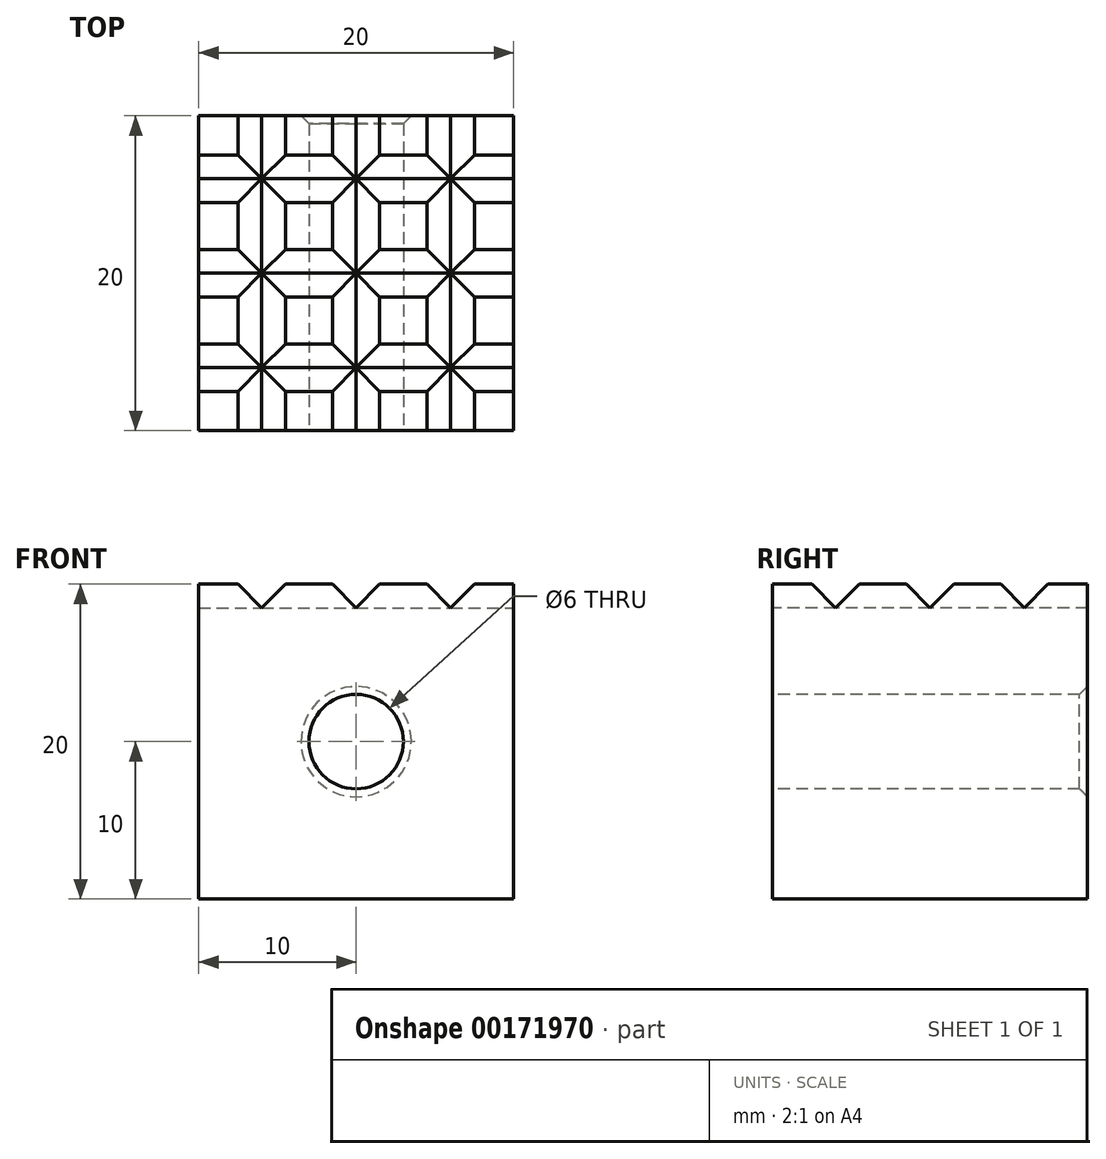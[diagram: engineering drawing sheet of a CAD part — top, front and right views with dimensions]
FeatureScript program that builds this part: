
annotation { "Feature Type Name" : "Feature", "Feature Type Description" : "" }
export const myFeature = defineFeature(function(context is Context, id is Id, definition is map)
    precondition{}
    {
        {
            var Q0;
            Q0=qCreatedBy(makeId("Top.planeOp"),FACE);
            var sketch = newSketch(context, id + "F0", { "sketchPlane" : qUnion([Q0])});
            skLineSegment(sketch, "E0.bottom", {"start": v(10, 10) * mm, "end": v(-10, 10) * mm});
            skLineSegment(sketch, "E0.top", {"start": v(10, -10) * mm, "end": v(-10, -10) * mm});
            skLineSegment(sketch, "E0.left", {"start": v(10, 10) * mm, "end": v(10, -10) * mm});
            skLineSegment(sketch, "E0.right", {"start": v(-10, 10) * mm, "end": v(-10, -10) * mm});
            skPoint(sketch, "E0.middle", {"position": v(0, 0) * mm});
            skSolve(sketch);
        }
        {
            var Q0;
            Q0 = qSketchRegion(id + "F0", true);
            extrude(context, id + "F1", {"entities" : qUnion([Q0]), "endBound" : BoundingType.SYMMETRIC, "depth" : 20 * mm});
        }
        {
            var Q0;
            Q0=makeQuery(id+"F1.opExtrude","SWEPT_FACE",FACE,{"disambiguationData":[OSD([sQuery(id+"F0.wireOp",EDGE,"E0.top")])]});
            var sketch = newSketch(context, id + "F2", { "sketchPlane" : qUnion([Q0])});
            skCircle(sketch, "E1", {"center": v(0, 0) * mm, "radius": 3 * mm});
            skSolve(sketch);
        }
        {
            var Q0;
            Q0=makeQuery(id+"F2.imprint","IMPRINT",FACE,{"disambiguationData":[TD([[makeQuery(id+"F2.imprint","IMPRINT",EDGE,{"derivedFrom":sQuery(id+"F2.wireOp",EDGE,"E1")}),1.0]])]});
            extrude(context, id + "F3", {"entities" : qUnion([Q0]), "operationType" : NewBodyOperationType.REMOVE, "oppositeDirection" : true, "depth" : 25 * mm});
        }
        {
            var Q0;
            Q0=makeQuery(id+"F3.boolean.opBoolean","COPY",EDGE,{"derivedFrom":makeQuery(id+"F3.opExtrude","CAP_EDGE",EDGE,{"disambiguationData":[OSD([sQuery(id+"F2.wireOp",EDGE,"E1")])],"isStart":true})});
            var Q1;
            Q1=makeQuery(id+"F3.boolean.opBoolean","INTERSECT",EDGE,{"derivedFrom":[makeQuery(id+"F1.opExtrude","SWEPT_FACE",FACE,{"disambiguationData":[OSD([sQuery(id+"F0.wireOp",EDGE,"E0.bottom")])]}),makeQuery(id+"F3.opExtrude","SWEPT_FACE",FACE,{"disambiguationData":[OSD([sQuery(id+"F2.wireOp",EDGE,"E1")])]})]});
            chamfer(context, id + "F4", {"entities" : qUnion([Q0, Q1]), "chamferType" : ChamferType.OFFSET_ANGLE, "width" : .5 * mm, "oppositeDirection" : false, "angle" : 45 * degree, "tangentPropagation" : true});
        }
        {
            var Q0;
            Q0=makeQuery(id+"F1.opExtrude","SWEPT_FACE",FACE,{"disambiguationData":[OSD([sQuery(id+"F0.wireOp",EDGE,"E0.top")])]});
            var sketch = newSketch(context, id + "F5", { "sketchPlane" : qUnion([Q0])});
            skLineSegment(sketch, "E2", {"start": v(4.5, 10) * mm, "end": v(6, 8.5) * mm});
            skLineSegment(sketch, "E3", {"start": v(6, 8.5) * mm, "end": v(7.5, 10) * mm});
            skLineSegment(sketch, "E4", {"start": v(7.5, 10) * mm, "end": v(4.5, 10) * mm});
            skLineSegment(sketch, "E5.1.0.0", {"start": v(1.5, 10) * mm, "end": v(-1.5, 10) * mm});
            skLineSegment(sketch, "E5.1.0.1", {"start": v(0, 8.5) * mm, "end": v(1.5, 10) * mm});
            skLineSegment(sketch, "E5.1.0.2", {"start": v(-1.5, 10) * mm, "end": v(0, 8.5) * mm});
            skLineSegment(sketch, "E5.2.0.0", {"start": v(-4.5, 10) * mm, "end": v(-7.5, 10) * mm});
            skLineSegment(sketch, "E5.2.0.1", {"start": v(-6, 8.5) * mm, "end": v(-4.5, 10) * mm});
            skLineSegment(sketch, "E5.2.0.2", {"start": v(-7.5, 10) * mm, "end": v(-6, 8.5) * mm});
            skLineSegment(sketch, "E5.direction1", {"start": v(6, 8.5) * mm, "end": v(0, 8.5) * mm, "construction": true});
            skSolve(sketch);
        }
        {
            var Q0;
            Q0 = qSketchRegion(id + "F5", true);
            extrude(context, id + "F6", {"entities" : qUnion([Q0]), "operationType" : NewBodyOperationType.REMOVE, "oppositeDirection" : true, "depth" : 25 * mm});
        }
        {
            var Q0;
            Q0=makeQuery(id+"F1.opExtrude","SWEPT_FACE",FACE,{"disambiguationData":[OSD([sQuery(id+"F0.wireOp",EDGE,"E0.left")])]});
            var sketch = newSketch(context, id + "F7", { "sketchPlane" : qUnion([Q0])});
            skLineSegment(sketch, "E6", {"start": v(4.5, 10) * mm, "end": v(6, 8.5) * mm});
            skLineSegment(sketch, "E7", {"start": v(6, 8.5) * mm, "end": v(7.5, 10) * mm});
            skLineSegment(sketch, "E8", {"start": v(7.5, 10) * mm, "end": v(4.5, 10) * mm});
            skLineSegment(sketch, "E9.1.0.0", {"start": v(1.5, 10) * mm, "end": v(-1.5, 10) * mm});
            skLineSegment(sketch, "E9.1.0.1", {"start": v(0, 8.5) * mm, "end": v(1.5, 10) * mm});
            skLineSegment(sketch, "E9.1.0.2", {"start": v(-1.5, 10) * mm, "end": v(0, 8.5) * mm});
            skLineSegment(sketch, "E9.2.0.0", {"start": v(-4.5, 10) * mm, "end": v(-7.5, 10) * mm});
            skLineSegment(sketch, "E9.2.0.1", {"start": v(-6, 8.5) * mm, "end": v(-4.5, 10) * mm});
            skLineSegment(sketch, "E9.2.0.2", {"start": v(-7.5, 10) * mm, "end": v(-6, 8.5) * mm});
            skLineSegment(sketch, "E9.direction1", {"start": v(6, 8.5) * mm, "end": v(0, 8.5) * mm, "construction": true});
            skSolve(sketch);
        }
        {
            var Q0;
            Q0=makeQuery(id+"F7.imprint","IMPRINT",FACE,{"disambiguationData":[TD([[makeQuery(id+"F7.imprint","IMPRINT",EDGE,{"derivedFrom":sQuery(id+"F7.wireOp",EDGE,"E9.2.0.0")}),1.0]])]});
            var Q1;
            Q1=makeQuery(id+"F7.imprint","IMPRINT",FACE,{"disambiguationData":[TD([[makeQuery(id+"F7.imprint","IMPRINT",EDGE,{"derivedFrom":sQuery(id+"F7.wireOp",EDGE,"E9.1.0.0")}),1.0]])]});
            var Q2;
            Q2=makeQuery(id+"F7.imprint","IMPRINT",FACE,{"disambiguationData":[TD([[makeQuery(id+"F7.imprint","IMPRINT",EDGE,{"derivedFrom":sQuery(id+"F7.wireOp",EDGE,"E6")}),1.0]])]});
            extrude(context, id + "F8", {"entities" : qUnion([Q0, Q1, Q2]), "operationType" : NewBodyOperationType.REMOVE, "oppositeDirection" : true, "depth" : 25 * mm});
        }
    });
